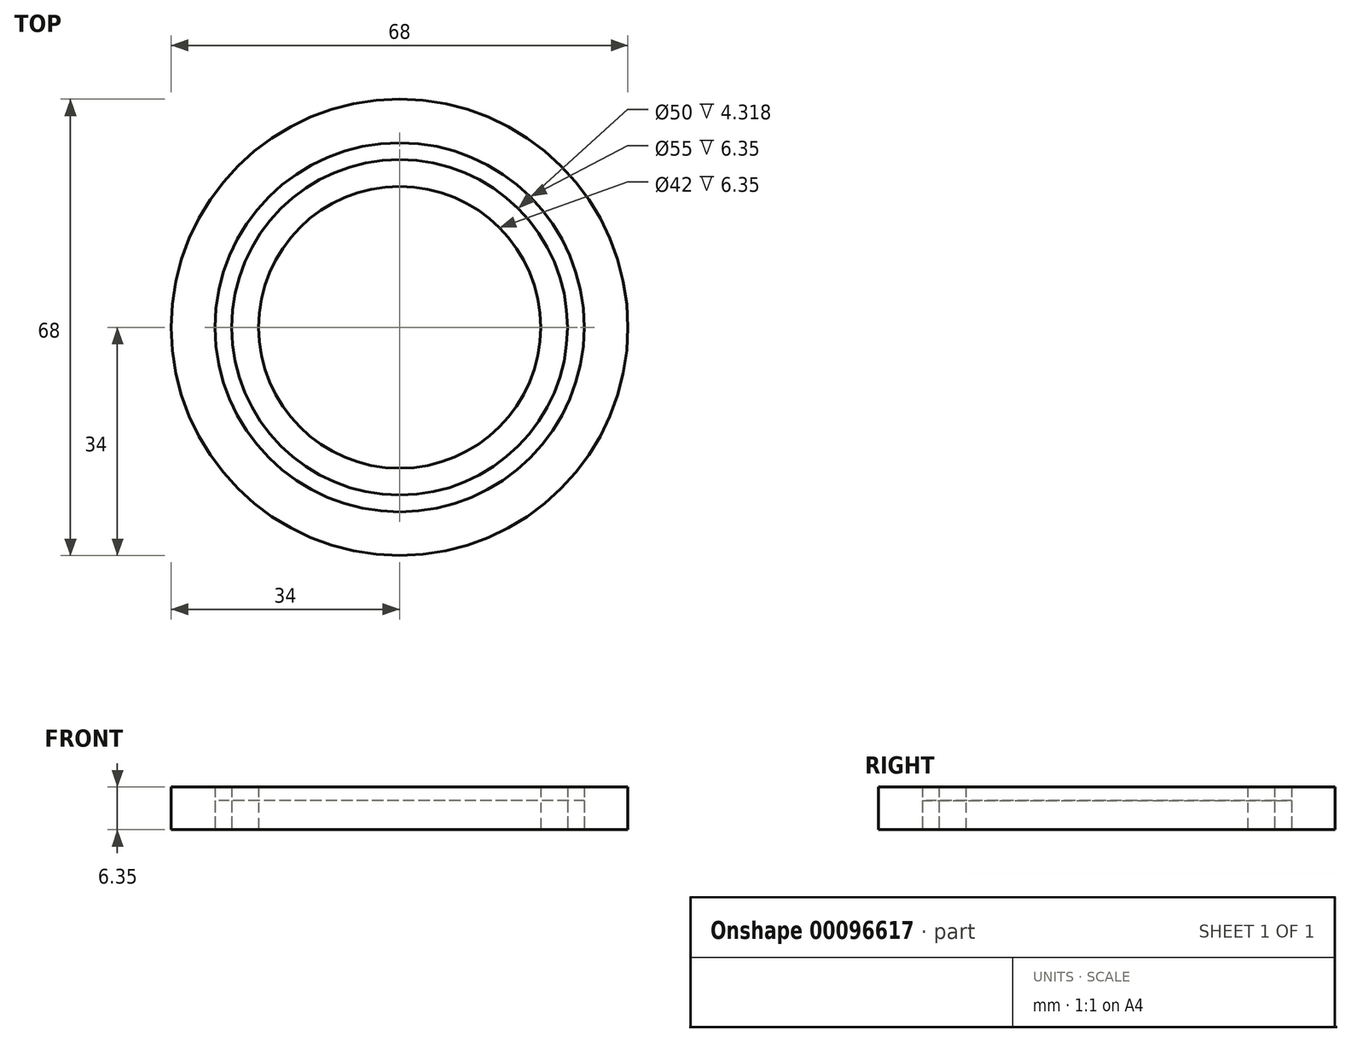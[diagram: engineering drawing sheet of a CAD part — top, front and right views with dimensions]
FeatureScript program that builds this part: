
annotation { "Feature Type Name" : "Feature", "Feature Type Description" : "" }
export const myFeature = defineFeature(function(context is Context, id is Id, definition is map)
    precondition{}
    {
        {
            var Q0;
            Q0=qCreatedBy(makeId("Top.planeOp"),FACE);
            var sketch = newSketch(context, id + "F0", { "sketchPlane" : qUnion([Q0])});
            skCircle(sketch, "E0", {"center": v(0, 0) * mm, "radius": 34 * mm});
            skCircle(sketch, "E1", {"center": v(0, 0) * mm, "radius": 21 * mm});
            skCircle(sketch, "E2", {"center": v(0, 0) * mm, "radius": 25 * mm});
            skCircle(sketch, "E3", {"center": v(0, 0) * mm, "radius": 27.5 * mm});
            skSolve(sketch);
        }
        {
            var Q0;
            Q0=makeQuery(id+"F0.imprint","IMPRINT",FACE,{"disambiguationData":[TD([[makeQuery(id+"F0.imprint","IMPRINT",EDGE,{"derivedFrom":sQuery(id+"F0.wireOp",EDGE,"E0")}),1.0]])]});
            var Q1;
            Q1=makeQuery(id+"F0.imprint","IMPRINT",FACE,{"disambiguationData":[TD([[makeQuery(id+"F0.imprint","IMPRINT",EDGE,{"derivedFrom":sQuery(id+"F0.wireOp",EDGE,"E1")}),-1.0]])]});
            extrude(context, id + "F1", {"entities" : qUnion([Q0, Q1]), "depth" : 6.35 * mm});
        }
        {
            var Q0;
            Q0=makeQuery(id+"F0.imprint","IMPRINT",FACE,{"disambiguationData":[TD([[makeQuery(id+"F0.imprint","IMPRINT",EDGE,{"derivedFrom":sQuery(id+"F0.wireOp",EDGE,"E2")}),-1.0]])]});
            extrude(context, id + "F2", {"entities" : qUnion([Q0]), "depth" : 4.32 * mm});
        }
    });
